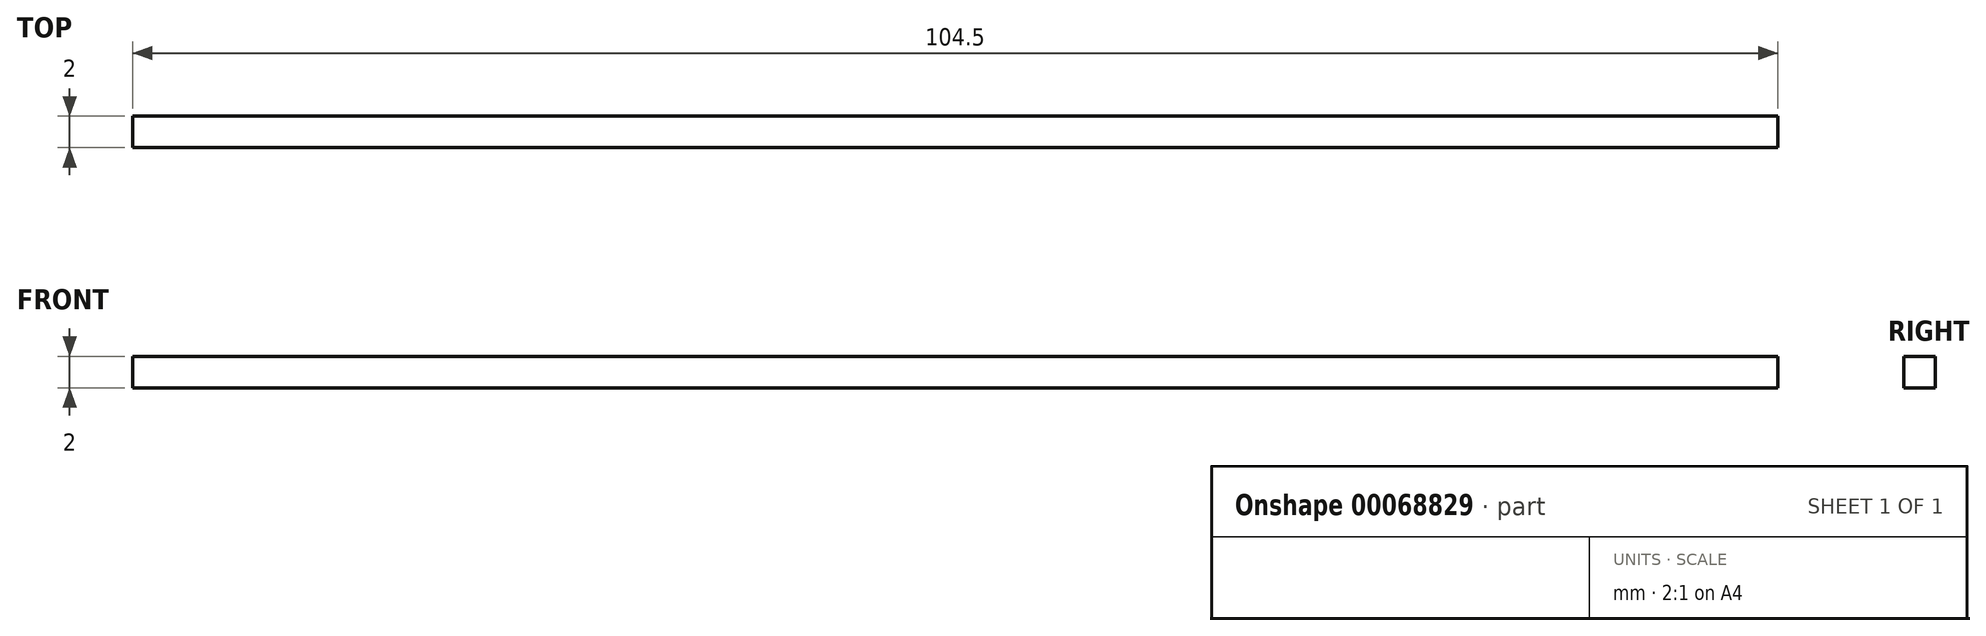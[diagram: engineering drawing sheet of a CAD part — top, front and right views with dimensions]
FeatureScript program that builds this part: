
annotation { "Feature Type Name" : "Feature", "Feature Type Description" : "" }
export const myFeature = defineFeature(function(context is Context, id is Id, definition is map)
    precondition{}
    {
        {
            var Q0;
            Q0=qCreatedBy(makeId("Top.planeOp"),FACE);
            var sketch = newSketch(context, id + "F0", { "sketchPlane" : qUnion([Q0])});
            skLineSegment(sketch, "E0.bottom", {"start": v(0, 0) * mm, "end": v(104.5, 0) * mm});
            skLineSegment(sketch, "E0.top", {"start": v(0, -2) * mm, "end": v(104.5, -2) * mm});
            skLineSegment(sketch, "E0.left", {"start": v(0, 0) * mm, "end": v(0, -2) * mm});
            skLineSegment(sketch, "E0.right", {"start": v(104.5, 0) * mm, "end": v(104.5, -2) * mm});
            skSolve(sketch);
        }
        {
            var Q0;
            Q0 = qSketchRegion(id + "F0", true);
            extrude(context, id + "F1", {"entities" : qUnion([Q0]), "depth" : 2 * mm});
        }
    });
